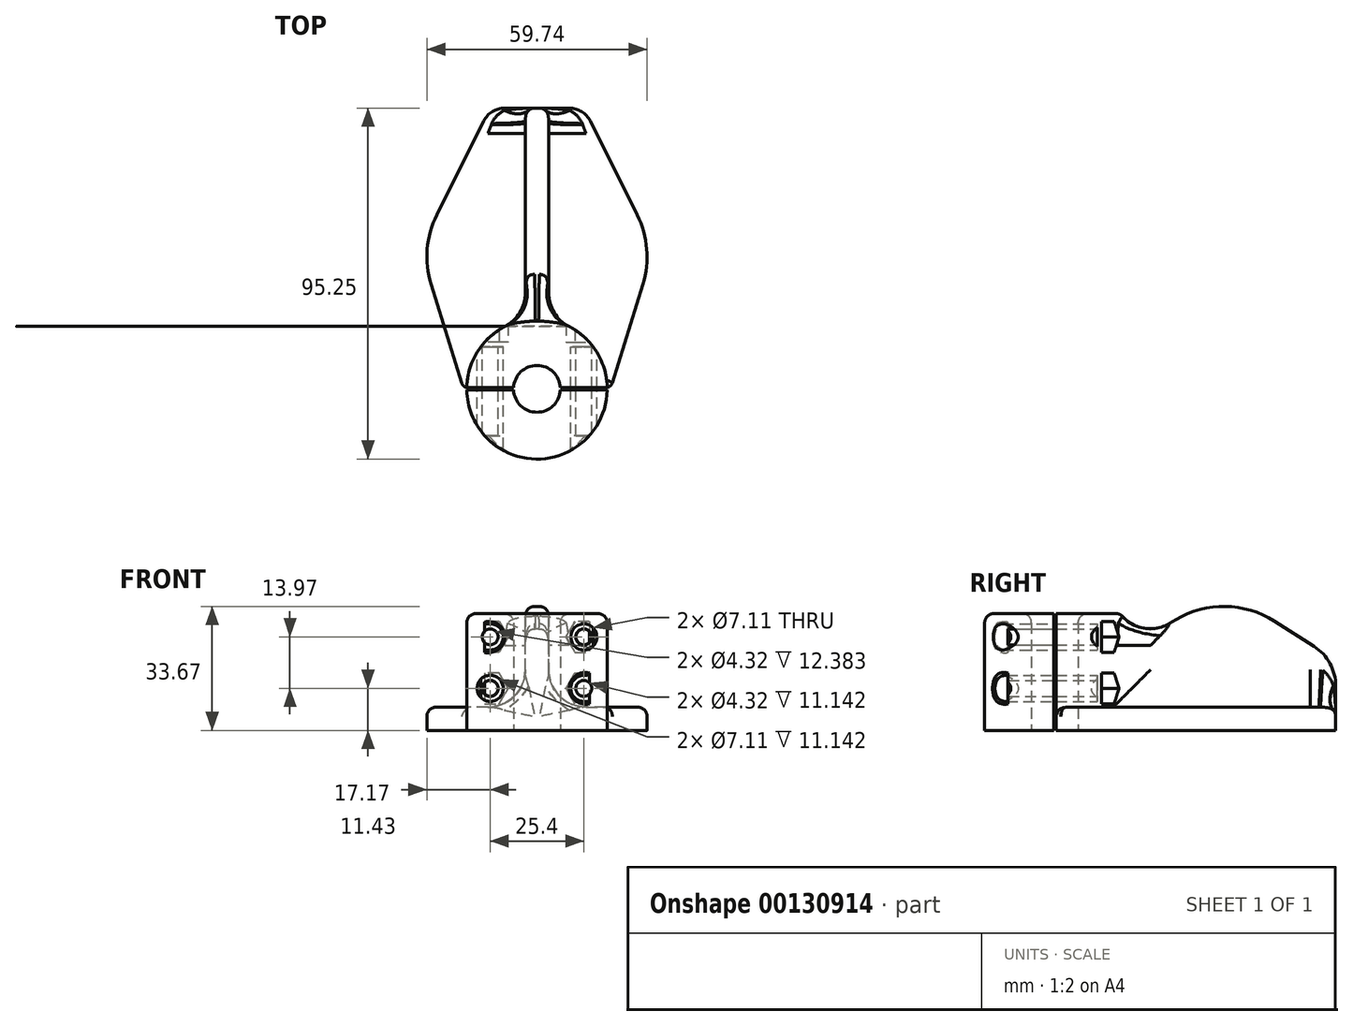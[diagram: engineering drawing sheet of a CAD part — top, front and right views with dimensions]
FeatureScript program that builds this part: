
annotation { "Feature Type Name" : "Feature", "Feature Type Description" : "" }
export const myFeature = defineFeature(function(context is Context, id is Id, definition is map)
    precondition{}
    {
        {
            var Q0;
            Q0=qCreatedBy(makeId("Top.planeOp"),FACE);
            var sketch = newSketch(context, id + "F0", { "sketchPlane" : qUnion([Q0])});
            skArc(sketch, "E0", {"start": v(-6.34, -0.32) * mm, "mid": v(0, -6.35) * mm, "end": v(6.34, -0.32) * mm});
            skLineSegment(sketch, "E1", {"start": v(51.79, -19.76) * mm, "end": v(0, -19.76) * mm});
            skLineSegment(sketch, "E2.MirrorCS", {"start": v(-51.79, -19.76) * mm, "end": v(0, -19.76) * mm});
            skArc(sketch, "E3", {"start": v(-19.05, -0.32) * mm, "mid": v(0, -19.05) * mm, "end": v(19.05, -0.32) * mm});
            skLineSegment(sketch, "E4", {"start": v(0, 76.2) * mm, "end": v(8.78, 76.2) * mm});
            skLineSegment(sketch, "E5", {"start": v(14.46, 72.69) * mm, "end": v(27.19, 47.23) * mm});
            skLineSegment(sketch, "E6", {"start": v(28.73, 28.35) * mm, "end": v(20.46, 1.66) * mm});
            skLineSegment(sketch, "E7", {"start": v(0, -19.76) * mm, "end": v(0, -61.3) * mm});
            skLineSegment(sketch, "E8.MirrorCS", {"start": v(0, 76.2) * mm, "end": v(-8.78, 76.2) * mm});
            skLineSegment(sketch, "E9.MirrorCS", {"start": v(-28.73, 28.35) * mm, "end": v(-20.46, 1.66) * mm});
            skLineSegment(sketch, "E10.MirrorCS", {"start": v(-14.46, 72.69) * mm, "end": v(-27.19, 47.23) * mm});
            skPoint(sketch, "E11.visualSharp", {"position": v(31.75, 38.1) * mm});
            skArc(sketch, "E11.filletArc", {"start": v(28.73, 28.35) * mm, "mid": v(29.78, 37.94) * mm, "end": v(27.19, 47.23) * mm});
            skPoint(sketch, "E12.visualSharp", {"position": v(-31.75, 38.1) * mm});
            skArc(sketch, "E12.filletArc", {"start": v(-27.19, 47.23) * mm, "mid": v(-29.78, 37.94) * mm, "end": v(-28.73, 28.35) * mm});
            skPoint(sketch, "E13.visualSharp", {"position": v(12.7, 76.2) * mm});
            skArc(sketch, "E13.filletArc", {"start": v(14.46, 72.69) * mm, "mid": v(12.11, 75.25) * mm, "end": v(8.78, 76.2) * mm});
            skPoint(sketch, "E14.visualSharp", {"position": v(-12.7, 76.2) * mm});
            skArc(sketch, "E14.filletArc", {"start": v(-8.78, 76.2) * mm, "mid": v(-12.11, 75.25) * mm, "end": v(-14.46, 72.69) * mm});
            skLineSegment(sketch, "E15", {"start": v(-24.66, 0) * mm, "end": v(25.12, 0) * mm});
            skLineSegment(sketch, "E16.0", {"start": v(-19.05, -0.32) * mm, "end": v(19.05, -0.32) * mm});
            skLineSegment(sketch, "E17.0", {"start": v(-18.64, 0.32) * mm, "end": v(18.64, 0.32) * mm});
            skArc(sketch, "E18.trimOffspring", {"start": v(6.34, 0.32) * mm, "mid": v(0, 6.35) * mm, "end": v(-6.34, 0.32) * mm});
            skArc(sketch, "E19.trimOffspring", {"start": v(19.05, 0.32) * mm, "mid": v(0, 19.05) * mm, "end": v(-19.05, 0.32) * mm});
            skPoint(sketch, "E20.visualSharp", {"position": v(-20.04, 0.32) * mm});
            skArc(sketch, "E20.filletArc", {"start": v(-20.46, 1.66) * mm, "mid": v(-19.77, 0.69) * mm, "end": v(-18.64, 0.32) * mm});
            skPoint(sketch, "E21.visualSharp", {"position": v(20.04, 0.32) * mm});
            skArc(sketch, "E21.filletArc", {"start": v(18.64, 0.32) * mm, "mid": v(19.77, 0.69) * mm, "end": v(20.46, 1.66) * mm});
            skSolve(sketch);
        }
        {
            var Q0;
            Q0=qCreatedBy(makeId("Right.planeOp"),FACE);
            var sketch = newSketch(context, id + "F1", { "sketchPlane" : qUnion([Q0])});
            skLineSegment(sketch, "E22", {"start": v(-14.29, 0) * mm, "end": v(-14.29, 19.05) * mm});
            skLineSegment(sketch, "E23", {"start": v(-14.29, 0) * mm, "end": v(76.2, 0) * mm});
            skPoint(sketch, "E24.visualSharp", {"position": v(46.35, 38.1) * mm});
            skLineSegment(sketch, "E25", {"start": v(76.2, 0) * mm, "end": v(76.2, 12.09) * mm});
            skLineSegment(sketch, "E26", {"start": v(70.33, 22.8) * mm, "end": v(59.54, 29.68) * mm});
            skLineSegment(sketch, "E27", {"start": v(-14.29, 19.05) * mm, "end": v(7.31, 19.05) * mm});
            skLineSegment(sketch, "E28", {"start": v(20.28, 22.61) * mm, "end": v(32.9, 30.1) * mm});
            skPoint(sketch, "E29.visualSharp", {"position": v(14.29, 19.05) * mm});
            skArc(sketch, "E29.filletArc", {"start": v(7.31, 19.05) * mm, "mid": v(14.04, 19.96) * mm, "end": v(20.28, 22.61) * mm});
            skPoint(sketch, "E30.visualSharp", {"position": v(46.36, 38.1) * mm});
            skArc(sketch, "E30.filletArc", {"start": v(59.54, 29.68) * mm, "mid": v(46.28, 33.67) * mm, "end": v(32.9, 30.1) * mm});
            skLineSegment(sketch, "E31", {"start": v(6.35, 0) * mm, "end": v(6.35, 19.05) * mm});
            skPoint(sketch, "E32.visualSharp", {"position": v(76.2, 19.05) * mm});
            skArc(sketch, "E32.filletArc", {"start": v(76.2, 12.09) * mm, "mid": v(74.64, 18.2) * mm, "end": v(70.33, 22.8) * mm});
            skSolve(sketch);
        }
        {
            var Q0;
            Q0=makeQuery(id+"F0.imprint","IMPRINT",FACE,{"disambiguationData":[TD([[makeQuery(id+"F0.imprint","IMPRINT",EDGE,{"derivedFrom":sQuery(id+"F0.wireOp",EDGE,"E0")}),-1.0]])]});
            extrude(context, id + "F2", {"entities" : qUnion([Q0]), "depth" : 31.75 * mm});
        }
        {
            var Q0;
            Q0=makeQuery(id+"F0.imprint","IMPRINT",FACE,{"disambiguationData":[TD([[makeQuery(id+"F0.imprint","IMPRINT",EDGE,{"derivedFrom":sQuery(id+"F0.wireOp",EDGE,"E4")}),-1.0]])]});
            extrude(context, id + "F3", {"entities" : qUnion([Q0]), "depth" : 6.35 * mm});
        }
        {
            var Q0;
            {var subQ3=sQuery(id+"F1.wireOp",EDGE,"E25");Q0=makeQuery(id+"F1.imprint","IMPRINT",FACE,{"disambiguationData":[TD([[makeQuery(id+"F1.imprint","IMPRINT",EDGE,{"derivedFrom":subQ3}),1.0]])]});}
            extrude(context, id + "F4", {"entities" : qUnion([Q0]), "depth" : 3.17 * mm, "hasSecondDirection" : true, "secondDirectionOppositeDirection" : true, "secondDirectionDepth" : 3.17 * mm});
        }
        {
            var Q0;
            {var subQ0=sQuery(id+"F0.wireOp",EDGE,"E18.trimOffspring");Q0=makeQuery(id+"F0.imprint","IMPRINT",FACE,{"disambiguationData":[TD([[makeQuery(id+"F0.imprint","IMPRINT",EDGE,{"derivedFrom":subQ0}),-1.0]])]});}
            extrude(context, id + "F5", {"entities" : qUnion([Q0]), "depth" : 31.75 * mm});
        }
        {
            var Q0;
            Q0=qCreatedBy(makeId("Front.planeOp"),FACE);
            var sketch = newSketch(context, id + "F6", { "sketchPlane" : qUnion([Q0])});
            skCircle(sketch, "E33", {"center": v(12.7, 11.43) * mm, "radius": 3.56 * mm});
            skCircle(sketch, "E34.cCircle", {"center": v(12.7, 11.43) * mm, "radius": 4.2 * mm, "construction": true});
            skLineSegment(sketch, "E34.0", {"start": v(10.28, 15.62) * mm, "end": v(15.12, 15.62) * mm});
            skLineSegment(sketch, "E34.1", {"start": v(15.12, 15.62) * mm, "end": v(17.54, 11.43) * mm});
            skLineSegment(sketch, "E34.2", {"start": v(17.54, 11.43) * mm, "end": v(15.12, 7.24) * mm});
            skLineSegment(sketch, "E34.3", {"start": v(15.12, 7.24) * mm, "end": v(10.28, 7.24) * mm});
            skLineSegment(sketch, "E34.4", {"start": v(10.28, 7.24) * mm, "end": v(7.86, 11.43) * mm});
            skLineSegment(sketch, "E34.5", {"start": v(7.86, 11.43) * mm, "end": v(10.28, 15.62) * mm});
            skPoint(sketch, "E34.0.midPoint", {"position": v(12.7, 15.62) * mm});
            skCircle(sketch, "E35", {"center": v(12.7, 11.43) * mm, "radius": 2.16 * mm});
            skLineSegment(sketch, "E36", {"start": v(0, 0) * mm, "end": v(0, 18.41) * mm});
            skLineSegment(sketch, "E37", {"start": v(0, 18.41) * mm, "end": v(27.72, 18.41) * mm});
            skPoint(sketch, "E38.MirrorP", {"position": v(12.7, 21.2) * mm});
            skLineSegment(sketch, "E39.MirrorCS", {"start": v(10.28, 29.6) * mm, "end": v(7.86, 25.4) * mm});
            skLineSegment(sketch, "E40.MirrorCS", {"start": v(15.12, 29.6) * mm, "end": v(10.28, 29.6) * mm});
            skLineSegment(sketch, "E41.MirrorCS", {"start": v(17.54, 25.4) * mm, "end": v(15.12, 29.6) * mm});
            skLineSegment(sketch, "E42.MirrorCS", {"start": v(10.28, 21.2) * mm, "end": v(15.12, 21.2) * mm});
            skLineSegment(sketch, "E43.MirrorCS", {"start": v(7.86, 25.4) * mm, "end": v(10.28, 21.2) * mm});
            skLineSegment(sketch, "E44.MirrorCS", {"start": v(15.12, 21.2) * mm, "end": v(17.54, 25.4) * mm});
            skCircle(sketch, "E45.MirrorC", {"center": v(12.7, 25.4) * mm, "radius": 2.16 * mm});
            skCircle(sketch, "E46.MirrorC", {"center": v(12.7, 25.4) * mm, "radius": 3.56 * mm});
            skCircle(sketch, "E47.MirrorC", {"center": v(12.7, 25.4) * mm, "radius": 4.2 * mm, "construction": true});
            skLineSegment(sketch, "E48.MirrorCS", {"start": v(-10.28, 15.62) * mm, "end": v(-15.12, 15.62) * mm});
            skLineSegment(sketch, "E49.MirrorCS", {"start": v(-15.12, 15.62) * mm, "end": v(-17.54, 11.43) * mm});
            skLineSegment(sketch, "E50.MirrorCS", {"start": v(-7.86, 25.4) * mm, "end": v(-10.28, 21.2) * mm});
            skCircle(sketch, "E51.MirrorC", {"center": v(-12.7, 25.4) * mm, "radius": 2.16 * mm});
            skCircle(sketch, "E52.MirrorC", {"center": v(-12.7, 25.4) * mm, "radius": 4.2 * mm, "construction": true});
            skLineSegment(sketch, "E53.MirrorCS", {"start": v(-15.12, 21.2) * mm, "end": v(-17.54, 25.4) * mm});
            skCircle(sketch, "E54.MirrorC", {"center": v(-12.7, 11.43) * mm, "radius": 2.16 * mm});
            skLineSegment(sketch, "E55.MirrorCS", {"start": v(-7.86, 11.43) * mm, "end": v(-10.28, 15.62) * mm});
            skLineSegment(sketch, "E56.MirrorCS", {"start": v(-10.28, 7.24) * mm, "end": v(-7.86, 11.43) * mm});
            skLineSegment(sketch, "E57.MirrorCS", {"start": v(-15.12, 7.24) * mm, "end": v(-10.28, 7.24) * mm});
            skCircle(sketch, "E58.MirrorC", {"center": v(-12.7, 11.43) * mm, "radius": 4.2 * mm, "construction": true});
            skPoint(sketch, "E59.MirrorP", {"position": v(-12.7, 15.62) * mm});
            skCircle(sketch, "E60.MirrorC", {"center": v(-12.7, 25.4) * mm, "radius": 3.56 * mm});
            skLineSegment(sketch, "E61.MirrorCS", {"start": v(-10.28, 29.6) * mm, "end": v(-7.86, 25.4) * mm});
            skLineSegment(sketch, "E62.MirrorCS", {"start": v(-17.54, 11.43) * mm, "end": v(-15.12, 7.24) * mm});
            skLineSegment(sketch, "E63.MirrorCS", {"start": v(-10.28, 21.2) * mm, "end": v(-15.12, 21.2) * mm});
            skPoint(sketch, "E64.MirrorP", {"position": v(-12.7, 21.2) * mm});
            skLineSegment(sketch, "E65.MirrorCS", {"start": v(-17.54, 25.4) * mm, "end": v(-15.12, 29.6) * mm});
            skLineSegment(sketch, "E66.MirrorCS", {"start": v(-15.12, 29.6) * mm, "end": v(-10.28, 29.6) * mm});
            skCircle(sketch, "E67.MirrorC", {"center": v(-12.7, 11.43) * mm, "radius": 3.56 * mm});
            skSolve(sketch);
        }
        {
            var Q0;
            Q0=makeQuery(id+"F6.imprint","IMPRINT",FACE,{"disambiguationData":[TD([[makeQuery(id+"F6.imprint","IMPRINT",EDGE,{"derivedFrom":sQuery(id+"F6.wireOp",EDGE,"E33")}),-1.0]])]});
            var Q1;
            Q1=makeQuery(id+"F6.imprint","IMPRINT",FACE,{"disambiguationData":[TD([[makeQuery(id+"F6.imprint","IMPRINT",EDGE,{"derivedFrom":sQuery(id+"F6.wireOp",EDGE,"E33")}),1.0]])]});
            var Q2;
            Q2=makeQuery(id+"F6.imprint","IMPRINT",FACE,{"disambiguationData":[TD([[makeQuery(id+"F6.imprint","IMPRINT",EDGE,{"derivedFrom":sQuery(id+"F6.wireOp",EDGE,"E35")}),1.0]])]});
            var Q3;
            Q3=makeQuery(id+"F6.imprint","IMPRINT",FACE,{"disambiguationData":[TD([[makeQuery(id+"F6.imprint","IMPRINT",EDGE,{"derivedFrom":sQuery(id+"F6.wireOp",EDGE,"E48.MirrorCS")}),1.0]])]});
            var Q4;
            Q4=makeQuery(id+"F6.imprint","IMPRINT",FACE,{"disambiguationData":[TD([[makeQuery(id+"F6.imprint","IMPRINT",EDGE,{"derivedFrom":sQuery(id+"F6.wireOp",EDGE,"E54.MirrorC")}),1.0]])]});
            var Q5;
            Q5=makeQuery(id+"F6.imprint","IMPRINT",FACE,{"disambiguationData":[TD([[makeQuery(id+"F6.imprint","IMPRINT",EDGE,{"derivedFrom":sQuery(id+"F6.wireOp",EDGE,"E54.MirrorC")}),-1.0]])]});
            var Q6;
            Q6=makeQuery(id+"F6.imprint","IMPRINT",FACE,{"disambiguationData":[TD([[makeQuery(id+"F6.imprint","IMPRINT",EDGE,{"derivedFrom":sQuery(id+"F6.wireOp",EDGE,"E50.MirrorCS")}),-1.0]])]});
            var Q7;
            Q7=makeQuery(id+"F6.imprint","IMPRINT",FACE,{"disambiguationData":[TD([[makeQuery(id+"F6.imprint","IMPRINT",EDGE,{"derivedFrom":sQuery(id+"F6.wireOp",EDGE,"E51.MirrorC")}),-1.0]])]});
            var Q8;
            Q8=makeQuery(id+"F6.imprint","IMPRINT",FACE,{"disambiguationData":[TD([[makeQuery(id+"F6.imprint","IMPRINT",EDGE,{"derivedFrom":sQuery(id+"F6.wireOp",EDGE,"E51.MirrorC")}),1.0]])]});
            var Q9;
            Q9=makeQuery(id+"F6.imprint","IMPRINT",FACE,{"disambiguationData":[TD([[makeQuery(id+"F6.imprint","IMPRINT",EDGE,{"derivedFrom":sQuery(id+"F6.wireOp",EDGE,"E39.MirrorCS")}),1.0]])]});
            var Q10;
            Q10=makeQuery(id+"F6.imprint","IMPRINT",FACE,{"disambiguationData":[TD([[makeQuery(id+"F6.imprint","IMPRINT",EDGE,{"derivedFrom":sQuery(id+"F6.wireOp",EDGE,"E45.MirrorC")}),1.0]])]});
            var Q11;
            Q11=makeQuery(id+"F6.imprint","IMPRINT",FACE,{"disambiguationData":[TD([[makeQuery(id+"F6.imprint","IMPRINT",EDGE,{"derivedFrom":sQuery(id+"F6.wireOp",EDGE,"E45.MirrorC")}),-1.0]])]});
            var Q12;
            Q12=makeQuery(id+"F6.imprint","IMPRINT",FACE,{"disambiguationData":[TD([[makeQuery(id+"F6.imprint","IMPRINT",EDGE,{"derivedFrom":sQuery(id+"F6.wireOp",EDGE,"E61.MirrorCS")}),1.0]])]});
            var Q13;
            Q13=makeQuery(id+"F6.imprint","IMPRINT",FACE,{"disambiguationData":[TD([[makeQuery(id+"F6.imprint","IMPRINT",EDGE,{"derivedFrom":sQuery(id+"F6.wireOp",EDGE,"E39.MirrorCS")}),-1.0]])]});
            var Q14;
            Q14=makeQuery(id+"F6.imprint","IMPRINT",FACE,{"disambiguationData":[TD([[makeQuery(id+"F6.imprint","IMPRINT",EDGE,{"derivedFrom":sQuery(id+"F6.wireOp",EDGE,"E34.0")}),1.0]])]});
            var Q15;
            Q15=makeQuery(id+"F6.imprint","IMPRINT",FACE,{"disambiguationData":[TD([[makeQuery(id+"F6.imprint","IMPRINT",EDGE,{"derivedFrom":sQuery(id+"F6.wireOp",EDGE,"E48.MirrorCS")}),-1.0]])]});
            extrude(context, id + "F7", {"entities" : qUnion([Q0, Q1, Q2, Q3, Q4, Q5, Q6, Q7, Q8, Q9, Q10, Q11, Q12, Q13, Q14, Q15]), "operationType" : NewBodyOperationType.REMOVE, "oppositeDirection" : true, "depth" : 33.65 * mm, "hasSecondDirection" : true, "secondDirectionOppositeDirection" : true, "secondDirectionDepth" : 12.7 * mm});
        }
        {
            var Q0;
            Q0=makeQuery(id+"F6.imprint","IMPRINT",FACE,{"disambiguationData":[TD([[makeQuery(id+"F6.imprint","IMPRINT",EDGE,{"derivedFrom":sQuery(id+"F6.wireOp",EDGE,"E33")}),1.0]])]});
            var Q1;
            Q1=makeQuery(id+"F6.imprint","IMPRINT",FACE,{"disambiguationData":[TD([[makeQuery(id+"F6.imprint","IMPRINT",EDGE,{"derivedFrom":sQuery(id+"F6.wireOp",EDGE,"E35")}),1.0]])]});
            var Q2;
            Q2=makeQuery(id+"F6.imprint","IMPRINT",FACE,{"disambiguationData":[TD([[makeQuery(id+"F6.imprint","IMPRINT",EDGE,{"derivedFrom":sQuery(id+"F6.wireOp",EDGE,"E54.MirrorC")}),1.0]])]});
            var Q3;
            Q3=makeQuery(id+"F6.imprint","IMPRINT",FACE,{"disambiguationData":[TD([[makeQuery(id+"F6.imprint","IMPRINT",EDGE,{"derivedFrom":sQuery(id+"F6.wireOp",EDGE,"E54.MirrorC")}),-1.0]])]});
            var Q4;
            Q4=makeQuery(id+"F6.imprint","IMPRINT",FACE,{"disambiguationData":[TD([[makeQuery(id+"F6.imprint","IMPRINT",EDGE,{"derivedFrom":sQuery(id+"F6.wireOp",EDGE,"E51.MirrorC")}),-1.0]])]});
            var Q5;
            Q5=makeQuery(id+"F6.imprint","IMPRINT",FACE,{"disambiguationData":[TD([[makeQuery(id+"F6.imprint","IMPRINT",EDGE,{"derivedFrom":sQuery(id+"F6.wireOp",EDGE,"E51.MirrorC")}),1.0]])]});
            var Q6;
            Q6=makeQuery(id+"F6.imprint","IMPRINT",FACE,{"disambiguationData":[TD([[makeQuery(id+"F6.imprint","IMPRINT",EDGE,{"derivedFrom":sQuery(id+"F6.wireOp",EDGE,"E45.MirrorC")}),1.0]])]});
            var Q7;
            Q7=makeQuery(id+"F6.imprint","IMPRINT",FACE,{"disambiguationData":[TD([[makeQuery(id+"F6.imprint","IMPRINT",EDGE,{"derivedFrom":sQuery(id+"F6.wireOp",EDGE,"E45.MirrorC")}),-1.0]])]});
            extrude(context, id + "F8", {"entities" : qUnion([Q0, Q1, Q2, Q3, Q4, Q5, Q6, Q7]), "operationType" : NewBodyOperationType.REMOVE, "depth" : 22.86 * mm, "hasSecondDirection" : true, "secondDirectionOppositeDirection" : false, "secondDirectionDepth" : 12.7 * mm});
        }
        {
            var Q0;
            Q0=makeQuery(id+"F6.imprint","IMPRINT",FACE,{"disambiguationData":[TD([[makeQuery(id+"F6.imprint","IMPRINT",EDGE,{"derivedFrom":sQuery(id+"F6.wireOp",EDGE,"E35")}),1.0]])]});
            var Q1;
            Q1=makeQuery(id+"F6.imprint","IMPRINT",FACE,{"disambiguationData":[TD([[makeQuery(id+"F6.imprint","IMPRINT",EDGE,{"derivedFrom":sQuery(id+"F6.wireOp",EDGE,"E54.MirrorC")}),-1.0]])]});
            var Q2;
            Q2=makeQuery(id+"F6.imprint","IMPRINT",FACE,{"disambiguationData":[TD([[makeQuery(id+"F6.imprint","IMPRINT",EDGE,{"derivedFrom":sQuery(id+"F6.wireOp",EDGE,"E51.MirrorC")}),1.0]])]});
            var Q3;
            Q3=makeQuery(id+"F6.imprint","IMPRINT",FACE,{"disambiguationData":[TD([[makeQuery(id+"F6.imprint","IMPRINT",EDGE,{"derivedFrom":sQuery(id+"F6.wireOp",EDGE,"E45.MirrorC")}),-1.0]])]});
            extrude(context, id + "F9", {"entities" : qUnion([Q0, Q1, Q2, Q3]), "depth" : 25.4 * mm, "hasSecondDirection" : true, "secondDirectionOppositeDirection" : true, "secondDirectionDepth" : 11.46 * mm});
        }
        {
            var Q0;
            Q0=makeQuery(id+"F3.opExtrude","SWEPT_BODY",BODY,{"disambiguationData":[OSD([sQuery(id+"F0.wireOp",EDGE,"E4"),sQuery(id+"F0.wireOp",EDGE,"E5"),sQuery(id+"F0.wireOp",EDGE,"E6"),sQuery(id+"F0.wireOp",EDGE,"E8.MirrorCS"),sQuery(id+"F0.wireOp",EDGE,"E9.MirrorCS"),sQuery(id+"F0.wireOp",EDGE,"E10.MirrorCS"),sQuery(id+"F0.wireOp",EDGE,"E11.filletArc"),sQuery(id+"F0.wireOp",EDGE,"E12.filletArc"),sQuery(id+"F0.wireOp",EDGE,"E13.filletArc"),sQuery(id+"F0.wireOp",EDGE,"E14.filletArc"),sQuery(id+"F0.wireOp",EDGE,"E19.trimOffspring"),sQuery(id+"F0.wireOp",EDGE,"E20.filletArc"),sQuery(id+"F0.wireOp",EDGE,"E21.filletArc")])]});
            var Q1;
            Q1=makeQuery(id+"F4.opExtrude","SWEPT_BODY",BODY,{"disambiguationData":[OSD([sQuery(id+"F1.wireOp",EDGE,"E23"),sQuery(id+"F1.wireOp",EDGE,"E25"),sQuery(id+"F1.wireOp",EDGE,"E26"),sQuery(id+"F1.wireOp",EDGE,"E27"),sQuery(id+"F1.wireOp",EDGE,"E28"),sQuery(id+"F1.wireOp",EDGE,"E29.filletArc"),sQuery(id+"F1.wireOp",EDGE,"E30.filletArc"),sQuery(id+"F1.wireOp",EDGE,"E31"),sQuery(id+"F1.wireOp",EDGE,"E32.filletArc")])]});
            var Q2;
            Q2=makeQuery(id+"F5.opExtrude","SWEPT_BODY",BODY,{"disambiguationData":[OSD([sQuery(id+"F0.wireOp",EDGE,"E17.0"),sQuery(id+"F0.wireOp",EDGE,"E18.trimOffspring"),sQuery(id+"F0.wireOp",EDGE,"E19.trimOffspring"),sQuery(id+"F0.wireOp",EDGE,"E20.filletArc"),sQuery(id+"F0.wireOp",EDGE,"E21.filletArc")])]});
            booleanBodies(context, id + "F10", {"operationType" : BooleanOperationType.UNION, "tools" : qUnion([Q0, Q1, Q2])});
        }
        {
            var Q0;
            Q0=makeQuery(id+"F9.opExtrude","SWEPT_BODY",BODY,{"disambiguationData":[OSD([sQuery(id+"F6.wireOp",EDGE,"E51.MirrorC")])]});
            var Q1;
            Q1=makeQuery(id+"F9.opExtrude","SWEPT_BODY",BODY,{"disambiguationData":[OSD([sQuery(id+"F6.wireOp",EDGE,"E54.MirrorC")])]});
            var Q2;
            Q2=makeQuery(id+"F9.opExtrude","SWEPT_BODY",BODY,{"disambiguationData":[OSD([sQuery(id+"F6.wireOp",EDGE,"E35")])]});
            var Q3;
            Q3=makeQuery(id+"F9.opExtrude","SWEPT_BODY",BODY,{"disambiguationData":[OSD([sQuery(id+"F6.wireOp",EDGE,"E45.MirrorC")])]});
            var Q4;
            Q4=makeQuery(id+"F2.opExtrude","SWEPT_BODY",BODY,{"disambiguationData":[OSD([sQuery(id+"F0.wireOp",EDGE,"E0"),sQuery(id+"F0.wireOp",EDGE,"E3"),sQuery(id+"F0.wireOp",EDGE,"E16.0")])]});
            var Q5;
            Q5=makeQuery(id+"F3.opExtrude","SWEPT_BODY",BODY,{"disambiguationData":[OSD([sQuery(id+"F0.wireOp",EDGE,"E4"),sQuery(id+"F0.wireOp",EDGE,"E5"),sQuery(id+"F0.wireOp",EDGE,"E6"),sQuery(id+"F0.wireOp",EDGE,"E8.MirrorCS"),sQuery(id+"F0.wireOp",EDGE,"E9.MirrorCS"),sQuery(id+"F0.wireOp",EDGE,"E10.MirrorCS"),sQuery(id+"F0.wireOp",EDGE,"E11.filletArc"),sQuery(id+"F0.wireOp",EDGE,"E12.filletArc"),sQuery(id+"F0.wireOp",EDGE,"E13.filletArc"),sQuery(id+"F0.wireOp",EDGE,"E14.filletArc"),sQuery(id+"F0.wireOp",EDGE,"E19.trimOffspring"),sQuery(id+"F0.wireOp",EDGE,"E20.filletArc"),sQuery(id+"F0.wireOp",EDGE,"E21.filletArc")])]});
            booleanBodies(context, id + "F11", {"operationType" : BooleanOperationType.SUBTRACTION, "tools" : qUnion([Q0, Q1, Q2, Q3]), "targets" : qUnion([Q4, Q5])});
        }
        {
            var Q0;
            Q0=makeQuery(id+"F2.opExtrude","CAP_EDGE",EDGE,{"disambiguationData":[OSD([sQuery(id+"F0.wireOp",EDGE,"E3")])],"isStart":false});
            var Q1;
            Q1=makeQuery(id+"F5.opExtrude","CAP_EDGE",EDGE,{"disambiguationData":[OSD([sQuery(id+"F0.wireOp",EDGE,"E19.trimOffspring")])],"isStart":false});
            var Q2;
            Q2=makeQuery(id+"F5.opExtrude","CAP_EDGE",EDGE,{"disambiguationData":[OSD([sQuery(id+"F0.wireOp",EDGE,"E18.trimOffspring")])],"isStart":false});
            var Q3;
            Q3=makeQuery(id+"F2.opExtrude","CAP_EDGE",EDGE,{"disambiguationData":[OSD([sQuery(id+"F0.wireOp",EDGE,"E0")])],"isStart":false});
            var Q4;
            Q4=makeQuery(id+"F4.opExtrude","CAP_EDGE",EDGE,{"disambiguationData":[OSD([sQuery(id+"F1.wireOp",EDGE,"E28")])],"isStart":true});
            var Q5;
            Q5=makeQuery(id+"F4.opExtrude","CAP_EDGE",EDGE,{"disambiguationData":[OSD([sQuery(id+"F1.wireOp",EDGE,"E28")])],"isStart":false});
            var Q6;
            Q6=makeQuery(id+"F3.opExtrude","CAP_EDGE",EDGE,{"disambiguationData":[OSD([sQuery(id+"F0.wireOp",EDGE,"E12.filletArc")])],"isStart":false});
            var Q7;
            Q7=makeQuery(id+"F3.opExtrude","CAP_EDGE",EDGE,{"disambiguationData":[OSD([sQuery(id+"F0.wireOp",EDGE,"E6")])],"isStart":false});
            fillet(context, id + "F12", {"entities" : qUnion([Q0, Q1, Q2, Q3, Q4, Q5, Q6, Q7]), "radius" : 2.54 * mm, "tangentPropagation" : true, "allowEdgeOverflow" : false});
        }
        {
            var Q0;
            Q0=makeQuery(id+"F12.opFillet","BLEND_EDGE",EDGE,{"blendedFrom":[makeQuery(id+"F4.opExtrude","CAP_EDGE",EDGE,{"disambiguationData":[OSD([sQuery(id+"F1.wireOp",EDGE,"E29.filletArc")])],"isStart":true}),makeQuery(id+"F5.opExtrude","SWEPT_FACE",FACE,{"disambiguationData":[OSD([sQuery(id+"F0.wireOp",EDGE,"E19.trimOffspring")])]})],"blendedInto":[makeQuery(id+"F5.opExtrude","SWEPT_FACE",FACE,{"disambiguationData":[OSD([sQuery(id+"F0.wireOp",EDGE,"E19.trimOffspring")])]})]});
            var Q1;
            {var subQ0=sQuery(id+"F0.wireOp",EDGE,"E19.trimOffspring");var subQ1=sQuery(id+"F0.wireOp",EDGE,"E20.filletArc");Q1=makeQuery(id+"F10.opBoolean","SPLIT",EDGE,{"disambiguationData":[TD([makeQuery(id+"F3.opExtrude","SWEPT_FACE",FACE,{"disambiguationData":[OSD([subQ1])]})])],"derivedFrom":makeQuery(id+"F3.opExtrude","CAP_EDGE",EDGE,{"disambiguationData":[OSD([subQ0])],"isStart":false})});}
            var Q2;
            {var subQ0=sQuery(id+"F0.wireOp",EDGE,"E19.trimOffspring");var subQ1=sQuery(id+"F0.wireOp",EDGE,"E21.filletArc");Q2=makeQuery(id+"F10.opBoolean","SPLIT",EDGE,{"disambiguationData":[TD([makeQuery(id+"F3.opExtrude","SWEPT_FACE",FACE,{"disambiguationData":[OSD([subQ1])]})])],"derivedFrom":makeQuery(id+"F3.opExtrude","CAP_EDGE",EDGE,{"disambiguationData":[OSD([subQ0])],"isStart":false})});}
            var Q3;
            Q3=makeQuery(id+"F10.opBoolean","INTERSECT",EDGE,{"derivedFrom":[makeQuery(id+"F3.opExtrude","CAP_FACE",FACE,{"disambiguationData":[OSD([sQuery(id+"F0.wireOp",EDGE,"E4"),sQuery(id+"F0.wireOp",EDGE,"E5"),sQuery(id+"F0.wireOp",EDGE,"E6"),sQuery(id+"F0.wireOp",EDGE,"E8.MirrorCS"),sQuery(id+"F0.wireOp",EDGE,"E9.MirrorCS"),sQuery(id+"F0.wireOp",EDGE,"E10.MirrorCS"),sQuery(id+"F0.wireOp",EDGE,"E11.filletArc"),sQuery(id+"F0.wireOp",EDGE,"E12.filletArc"),sQuery(id+"F0.wireOp",EDGE,"E13.filletArc"),sQuery(id+"F0.wireOp",EDGE,"E14.filletArc"),sQuery(id+"F0.wireOp",EDGE,"E19.trimOffspring"),sQuery(id+"F0.wireOp",EDGE,"E20.filletArc"),sQuery(id+"F0.wireOp",EDGE,"E21.filletArc")])],"isStart":false}),makeQuery(id+"F4.opExtrude","CAP_FACE",FACE,{"disambiguationData":[OSD([sQuery(id+"F1.wireOp",EDGE,"E23"),sQuery(id+"F1.wireOp",EDGE,"E25"),sQuery(id+"F1.wireOp",EDGE,"E26"),sQuery(id+"F1.wireOp",EDGE,"E27"),sQuery(id+"F1.wireOp",EDGE,"E28"),sQuery(id+"F1.wireOp",EDGE,"E29.filletArc"),sQuery(id+"F1.wireOp",EDGE,"E30.filletArc"),sQuery(id+"F1.wireOp",EDGE,"E31"),sQuery(id+"F1.wireOp",EDGE,"E32.filletArc")])],"isStart":false})]});
            var Q4;
            Q4=makeQuery(id+"F10.opBoolean","INTERSECT",EDGE,{"derivedFrom":[makeQuery(id+"F3.opExtrude","CAP_FACE",FACE,{"disambiguationData":[OSD([sQuery(id+"F0.wireOp",EDGE,"E4"),sQuery(id+"F0.wireOp",EDGE,"E5"),sQuery(id+"F0.wireOp",EDGE,"E6"),sQuery(id+"F0.wireOp",EDGE,"E8.MirrorCS"),sQuery(id+"F0.wireOp",EDGE,"E9.MirrorCS"),sQuery(id+"F0.wireOp",EDGE,"E10.MirrorCS"),sQuery(id+"F0.wireOp",EDGE,"E11.filletArc"),sQuery(id+"F0.wireOp",EDGE,"E12.filletArc"),sQuery(id+"F0.wireOp",EDGE,"E13.filletArc"),sQuery(id+"F0.wireOp",EDGE,"E14.filletArc"),sQuery(id+"F0.wireOp",EDGE,"E19.trimOffspring"),sQuery(id+"F0.wireOp",EDGE,"E20.filletArc"),sQuery(id+"F0.wireOp",EDGE,"E21.filletArc")])],"isStart":false}),makeQuery(id+"F4.opExtrude","CAP_FACE",FACE,{"disambiguationData":[OSD([sQuery(id+"F1.wireOp",EDGE,"E23"),sQuery(id+"F1.wireOp",EDGE,"E25"),sQuery(id+"F1.wireOp",EDGE,"E26"),sQuery(id+"F1.wireOp",EDGE,"E27"),sQuery(id+"F1.wireOp",EDGE,"E28"),sQuery(id+"F1.wireOp",EDGE,"E29.filletArc"),sQuery(id+"F1.wireOp",EDGE,"E30.filletArc"),sQuery(id+"F1.wireOp",EDGE,"E31"),sQuery(id+"F1.wireOp",EDGE,"E32.filletArc")])],"isStart":true})]});
            fillet(context, id + "F13", {"entities" : qUnion([Q0, Q1, Q2, Q3, Q4]), "radius" : 10.16 * mm, "tangentPropagation" : true, "allowEdgeOverflow" : false});
        }
        {
            var Q0;
            Q0=makeQuery(id+"F8.boolean.opBoolean","INTERSECT",EDGE,{"derivedFrom":[makeQuery(id+"F2.opExtrude","SWEPT_FACE",FACE,{"disambiguationData":[OSD([sQuery(id+"F0.wireOp",EDGE,"E3")])]}),makeQuery(id+"F8.opExtrude","SWEPT_FACE",FACE,{"disambiguationData":[OSD([sQuery(id+"F6.wireOp",EDGE,"E60.MirrorC")])]})]});
            var Q1;
            Q1=makeQuery(id+"F8.boolean.opBoolean","INTERSECT",EDGE,{"derivedFrom":[makeQuery(id+"F2.opExtrude","SWEPT_FACE",FACE,{"disambiguationData":[OSD([sQuery(id+"F0.wireOp",EDGE,"E3")])]}),makeQuery(id+"F8.opExtrude","SWEPT_FACE",FACE,{"disambiguationData":[OSD([sQuery(id+"F6.wireOp",EDGE,"E67.MirrorC")])]})]});
            var Q2;
            Q2=makeQuery(id+"F8.boolean.opBoolean","INTERSECT",EDGE,{"derivedFrom":[makeQuery(id+"F2.opExtrude","SWEPT_FACE",FACE,{"disambiguationData":[OSD([sQuery(id+"F0.wireOp",EDGE,"E3")])]}),makeQuery(id+"F8.opExtrude","SWEPT_FACE",FACE,{"disambiguationData":[OSD([sQuery(id+"F6.wireOp",EDGE,"E46.MirrorC")])]})]});
            var Q3;
            Q3=makeQuery(id+"F8.boolean.opBoolean","INTERSECT",EDGE,{"derivedFrom":[makeQuery(id+"F2.opExtrude","SWEPT_FACE",FACE,{"disambiguationData":[OSD([sQuery(id+"F0.wireOp",EDGE,"E3")])]}),makeQuery(id+"F8.opExtrude","SWEPT_FACE",FACE,{"disambiguationData":[OSD([sQuery(id+"F6.wireOp",EDGE,"E33")])]})]});
            fillet(context, id + "F14", {"entities" : qUnion([Q0, Q1, Q2, Q3]), "radius" : 0.76 * mm, "tangentPropagation" : true, "allowEdgeOverflow" : false});
        }
    });
